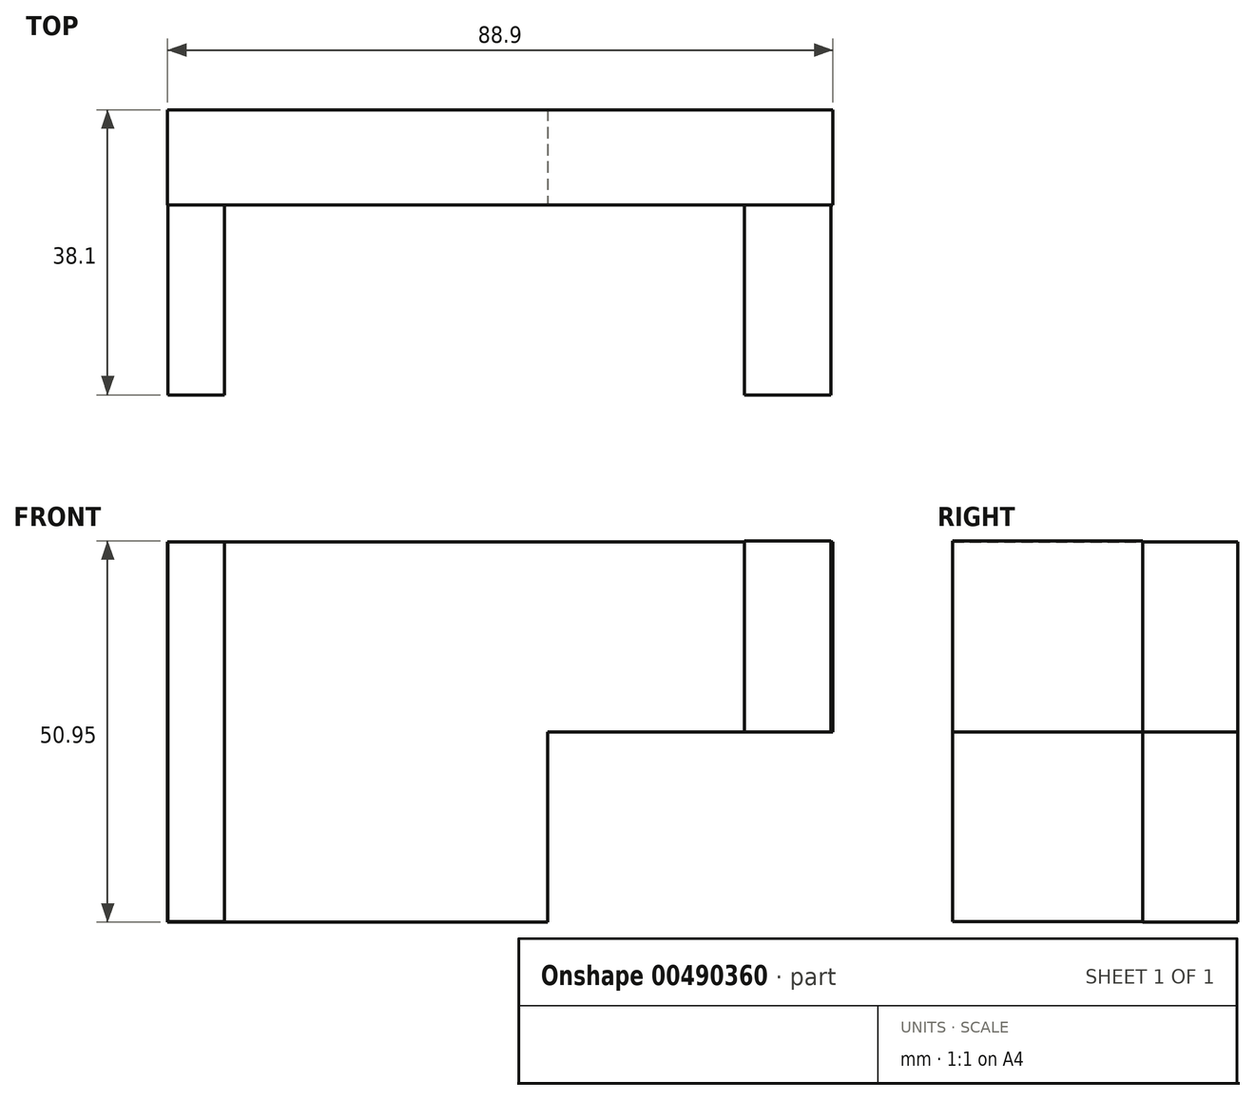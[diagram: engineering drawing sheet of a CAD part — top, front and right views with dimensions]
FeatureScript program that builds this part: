
annotation { "Feature Type Name" : "Feature", "Feature Type Description" : "" }
export const myFeature = defineFeature(function(context is Context, id is Id, definition is map)
    precondition{}
    {
        {
            var Q0;
            Q0=qCreatedBy(makeId("Front.planeOp"),FACE);
            var sketch = newSketch(context, id + "F0", { "sketchPlane" : qUnion([Q0])});
            skLineSegment(sketch, "E0.bottom", {"start": v(44.45, -25.4) * mm, "end": v(-44.45, -25.4) * mm});
            skLineSegment(sketch, "E0.top", {"start": v(44.45, 25.4) * mm, "end": v(-44.45, 25.4) * mm});
            skLineSegment(sketch, "E0.left", {"start": v(44.45, -25.4) * mm, "end": v(44.45, 25.4) * mm});
            skLineSegment(sketch, "E0.right", {"start": v(-44.45, -25.4) * mm, "end": v(-44.45, 25.4) * mm});
            skPoint(sketch, "E0.middle", {"position": v(0, 0) * mm});
            skSolve(sketch);
        }
        {
            var Q0;
            Q0 = qSketchRegion(id + "F0", true);
            extrude(context, id + "F1", {"entities" : qUnion([Q0]), "depth" : 12.7 * mm});
        }
        {
            var Q0;
            Q0 = qSketchRegion(id + "F0", true);
            extrude(context, id + "F2", {"entities" : qUnion([Q0]), "operationType" : NewBodyOperationType.ADD, "depth" : 12.7 * mm});
        }
        {
            var Q0;
            Q0=makeQuery(id+"F1.opExtrude","CAP_FACE",FACE,{"disambiguationData":[OSD([sQuery(id+"F0.wireOp",EDGE,"E0.bottom"),sQuery(id+"F0.wireOp",EDGE,"E0.top"),sQuery(id+"F0.wireOp",EDGE,"E0.left"),sQuery(id+"F0.wireOp",EDGE,"E0.right")])],"isStart":false});
            var sketch = newSketch(context, id + "F3", { "sketchPlane" : qUnion([Q0])});
            skLineSegment(sketch, "E1.bottom", {"start": v(44.45, -25.4) * mm, "end": v(6.35, -25.4) * mm});
            skLineSegment(sketch, "E1.top", {"start": v(44.45, 0) * mm, "end": v(6.35, 0) * mm});
            skLineSegment(sketch, "E1.left", {"start": v(44.45, -25.4) * mm, "end": v(44.45, 0) * mm});
            skLineSegment(sketch, "E1.right", {"start": v(6.35, -25.4) * mm, "end": v(6.35, 0) * mm});
            skSolve(sketch);
        }
        {
            var Q0;
            Q0 = qSketchRegion(id + "F3", true);
            extrude(context, id + "F4", {"entities" : qUnion([Q0]), "operationType" : NewBodyOperationType.REMOVE, "endBound" : BoundingType.THROUGH_ALL, "oppositeDirection" : true, "depth" : 25.4 * mm});
        }
        {
            var Q0;
            Q0=makeQuery(id+"F1.opExtrude","CAP_FACE",FACE,{"disambiguationData":[OSD([sQuery(id+"F0.wireOp",EDGE,"E0.bottom"),sQuery(id+"F0.wireOp",EDGE,"E0.top"),sQuery(id+"F0.wireOp",EDGE,"E0.left"),sQuery(id+"F0.wireOp",EDGE,"E0.right")])],"isStart":false});
            var sketch = newSketch(context, id + "F5", { "sketchPlane" : qUnion([Q0])});
            skCircle(sketch, "E2", {"center": v(6.35, 11.26) * mm, "radius": 3.53 * mm});
            skSolve(sketch);
        }
        {
            var Q0;
            Q0=makeQuery(id+"F5.imprint","IMPRINT",FACE,{"disambiguationData":[TD([[makeQuery(id+"F5.imprint","IMPRINT",EDGE,{"derivedFrom":sQuery(id+"F5.wireOp",EDGE,"E2")}),-1.0]])]});
            var sketch = newSketch(context, id + "F6", { "sketchPlane" : qUnion([Q0])});
            skLineSegment(sketch, "E3.bottom", {"start": v(-44.38, -25.34) * mm, "end": v(-36.86, -25.34) * mm});
            skLineSegment(sketch, "E3.top", {"start": v(-44.38, 25.39) * mm, "end": v(-36.86, 25.39) * mm});
            skLineSegment(sketch, "E3.left", {"start": v(-44.38, -25.34) * mm, "end": v(-44.38, 25.39) * mm});
            skLineSegment(sketch, "E3.right", {"start": v(-36.86, -25.34) * mm, "end": v(-36.86, 25.39) * mm});
            skSolve(sketch);
        }
        {
            var Q0;
            Q0 = qSketchRegion(id + "F6", true);
            extrude(context, id + "F7", {"entities" : qUnion([Q0]), "operationType" : NewBodyOperationType.ADD, "depth" : 25.4 * mm});
        }
        {
            var Q0;
            Q0=makeQuery(id+"F5.imprint","IMPRINT",FACE,{"disambiguationData":[TD([[makeQuery(id+"F5.imprint","IMPRINT",EDGE,{"derivedFrom":sQuery(id+"F5.wireOp",EDGE,"E2")}),-1.0]])]});
            var sketch = newSketch(context, id + "F8", { "sketchPlane" : qUnion([Q0])});
            skLineSegment(sketch, "E4.bottom", {"start": v(44.17, 0) * mm, "end": v(32.64, 0) * mm});
            skLineSegment(sketch, "E4.top", {"start": v(44.17, 25.55) * mm, "end": v(32.64, 25.55) * mm});
            skLineSegment(sketch, "E4.left", {"start": v(44.17, 0) * mm, "end": v(44.17, 25.55) * mm});
            skLineSegment(sketch, "E4.right", {"start": v(32.64, 0) * mm, "end": v(32.64, 25.55) * mm});
            skSolve(sketch);
        }
        {
            var Q0;
            Q0 = qSketchRegion(id + "F8", true);
            extrude(context, id + "F9", {"entities" : qUnion([Q0]), "operationType" : NewBodyOperationType.ADD, "depth" : 25.4 * mm});
        }
    });
